# Revit family: Estrichüberdecktes Kanalsystem EÜK_Kanal-Endverschlussstück
name_source: partatom
category: Generic Models
revit_build: Autodesk Revit 2015 (Build: 20140606_1530(x64)
units: mm (PartAtom-declared; Revit-internal decimal feet)

## types (9) — shared parameters
Length = 31 mm
Manufacturer = OBO Bettermann
Material = Steel, Galvanized
URL = http://www.obo-bettermann.com

## per-type parameters (varying)
| type | GTIN | Height | Manufacturer Art. No. | Width |
| SES 19027 | 4012195098829 | 27 mm  [stored 0.0885827 ft] | 7403980 | 190 mm |
| SES 25027 | 4012195098874 | 27 mm  [stored 0.0885827 ft] | 7404002 | 250 mm  [stored 0.82021 ft] |
| SES 19037 | 4012195098850 | 39 mm  [stored 0.127953 ft] | 7403984 | 190 mm |
| SES 19048 | 4012195098867 | 48 mm  [stored 0.15748 ft] | 7403988 | 190 mm |
| SES 25037 | 4012195098881 | 37 mm  [stored 0.121391 ft] | 7404006 | 250 mm  [stored 0.82021 ft] |
| SES 25048 | 4012195098911 | 48 mm  [stored 0.15748 ft] | 7404010 | 250 mm  [stored 0.82021 ft] |
| SES 35027 | 4012195098928 | 27 mm  [stored 0.0885827 ft] | 7404014 | 350 mm  [stored 1.14829 ft] |
| SES 35037 | 4012195098935 | 37 mm  [stored 0.121391 ft] | 7404018 | 350 mm  [stored 1.14829 ft] |
| SES 35048 | 4012195098942 | 48 mm  [stored 0.15748 ft] | 7404022 | 350 mm  [stored 1.14829 ft] |

note: column(s) folded — value = type name in every type: Article Type

note: [stored X ft] marks values corroborated as IEEE doubles in the binary element streams (Revit-internal decimal feet)

## geometry (parser evidence)
native form markers: Sweep x2
no freeform markers — native parametric forms only
